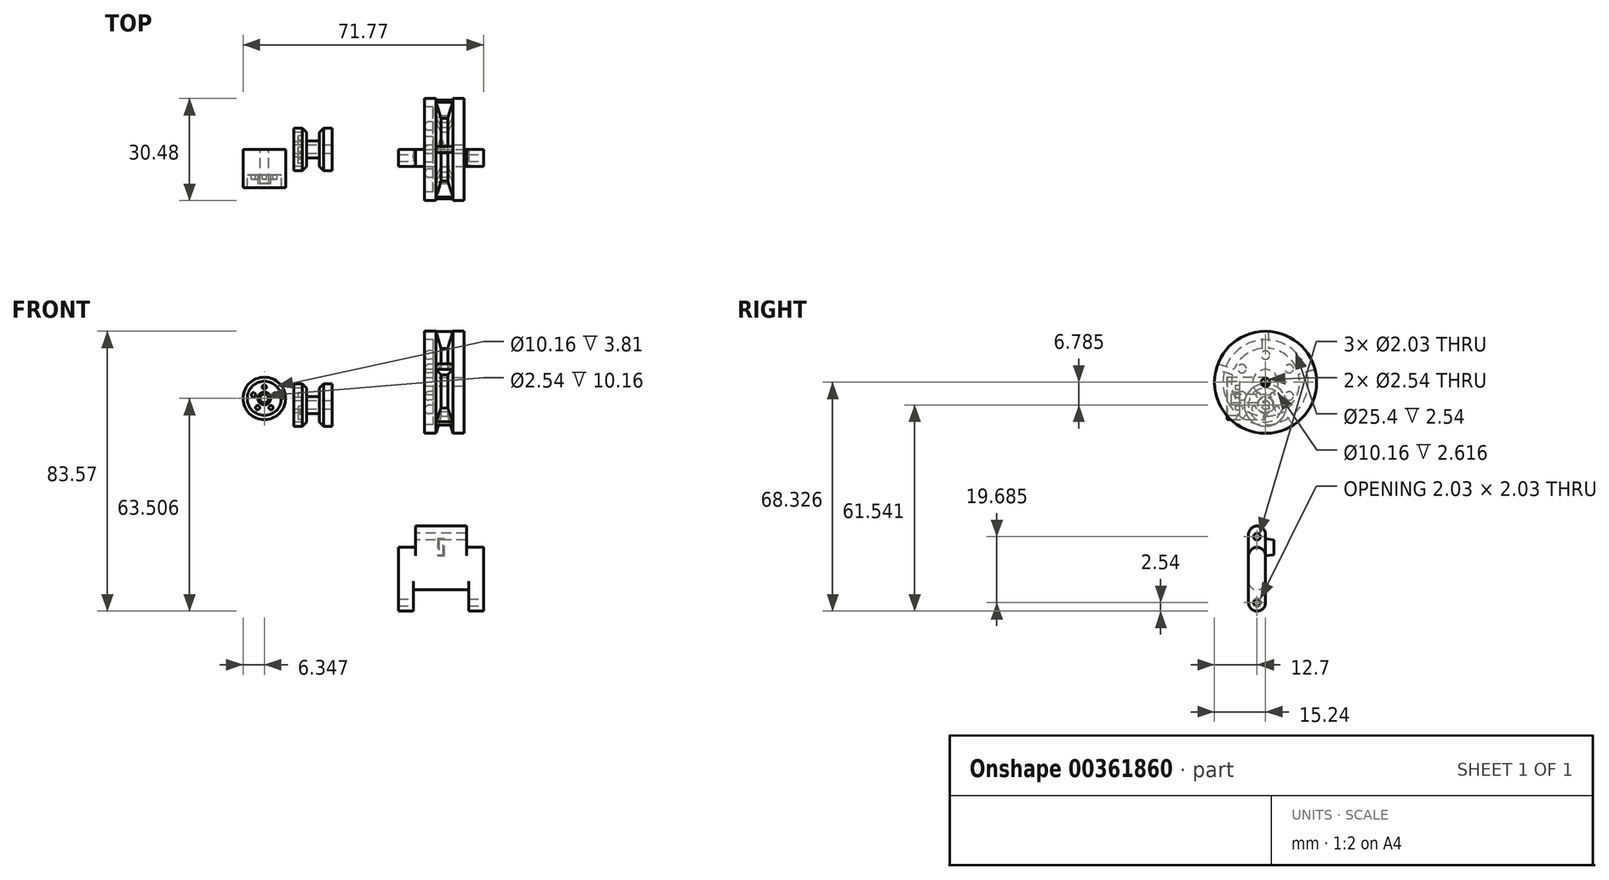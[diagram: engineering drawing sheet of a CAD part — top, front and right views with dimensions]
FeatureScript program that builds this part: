
annotation { "Feature Type Name" : "Feature", "Feature Type Description" : "" }
export const myFeature = defineFeature(function(context is Context, id is Id, definition is map)
    precondition{}
    {
        {
            var Q0;
            Q0=qCreatedBy(makeId("Front.planeOp"),FACE);
            var sketch = newSketch(context, id + "F0", { "sketchPlane" : qUnion([Q0])});
            skLineSegment(sketch, "E0", {"start": v(0, 6.35) * mm, "end": v(-7.62, 6.35) * mm});
            skLineSegment(sketch, "E1", {"start": v(-7.62, 6.35) * mm, "end": v(-7.62, 0) * mm});
            skLineSegment(sketch, "E2", {"start": v(-7.62, 0) * mm, "end": v(-12.7, 0) * mm});
            skLineSegment(sketch, "E3", {"start": v(-12.7, 0) * mm, "end": v(-12.7, -19.05) * mm});
            skLineSegment(sketch, "E4", {"start": v(-12.7, -19.05) * mm, "end": v(-8.26, -19.05) * mm});
            skLineSegment(sketch, "E5", {"start": v(-8.26, -19.05) * mm, "end": v(-8.26, -12.7) * mm});
            skLineSegment(sketch, "E6", {"start": v(-8.26, -12.7) * mm, "end": v(0, -12.7) * mm});
            skLineSegment(sketch, "E7.MirrorCS", {"start": v(0, 6.35) * mm, "end": v(7.62, 6.35) * mm});
            skLineSegment(sketch, "E8.MirrorCS", {"start": v(7.62, 6.35) * mm, "end": v(7.62, 0) * mm});
            skLineSegment(sketch, "E9.MirrorCS", {"start": v(7.62, 0) * mm, "end": v(12.7, 0) * mm});
            skLineSegment(sketch, "E10.MirrorCS", {"start": v(12.7, 0) * mm, "end": v(12.7, -19.05) * mm});
            skLineSegment(sketch, "E11.MirrorCS", {"start": v(12.7, -19.05) * mm, "end": v(8.26, -19.05) * mm});
            skLineSegment(sketch, "E12.MirrorCS", {"start": v(8.26, -12.7) * mm, "end": v(0, -12.7) * mm});
            skLineSegment(sketch, "E13.MirrorCS", {"start": v(8.26, -19.05) * mm, "end": v(8.26, -12.7) * mm});
            skSolve(sketch);
        }
        {
            var Q0;
            Q0=makeQuery(id+"F0.imprint","IMPRINT",FACE,{"disambiguationData":[TD([[makeQuery(id+"F0.imprint","IMPRINT",EDGE,{"derivedFrom":sQuery(id+"F0.wireOp",EDGE,"E0")}),1.0]])]});
            extrude(context, id + "F1", {"entities" : qUnion([Q0]), "depth" : 5.08 * mm});
        }
        {
            var Q0;
            Q0=makeQuery(id+"F1.opExtrude","SWEPT_FACE",FACE,{"disambiguationData":[OSD([sQuery(id+"F0.wireOp",EDGE,"E1")])]});
            var sketch = newSketch(context, id + "F2", { "sketchPlane" : qUnion([Q0])});
            skCircle(sketch, "E14", {"center": v(2.54, 3.17) * mm, "radius": 1.02 * mm});
            skPoint(sketch, "E14.centerSnap0", {"position": v(2.54, 6.35) * mm});
            skPoint(sketch, "E14.centerSnap1", {"position": v(5.08, 3.17) * mm});
            skSolve(sketch);
        }
        {
            var Q0;
            Q0=makeQuery(id+"F2.imprint","IMPRINT",FACE,{"disambiguationData":[TD([[makeQuery(id+"F2.imprint","IMPRINT",EDGE,{"derivedFrom":sQuery(id+"F2.wireOp",EDGE,"E14")}),1.0]])]});
            extrude(context, id + "F3", {"entities" : qUnion([Q0]), "operationType" : NewBodyOperationType.REMOVE, "oppositeDirection" : true, "depth" : 25.4 * mm});
        }
        {
            var Q0;
            Q0=makeQuery(id+"F1.opExtrude","CAP_EDGE",EDGE,{"disambiguationData":[OSD([sQuery(id+"F0.wireOp",EDGE,"E0"),sQuery(id+"F0.wireOp",EDGE,"E7.MirrorCS")])],"isStart":false});
            var Q1;
            Q1=makeQuery(id+"F1.opExtrude","CAP_EDGE",EDGE,{"disambiguationData":[OSD([sQuery(id+"F0.wireOp",EDGE,"E0"),sQuery(id+"F0.wireOp",EDGE,"E7.MirrorCS")])],"isStart":true});
            var Q2;
            Q2=makeQuery(id+"F1.opExtrude","CAP_EDGE",EDGE,{"disambiguationData":[OSD([sQuery(id+"F0.wireOp",EDGE,"E2")])],"isStart":false});
            var Q3;
            Q3=makeQuery(id+"F1.opExtrude","CAP_EDGE",EDGE,{"disambiguationData":[OSD([sQuery(id+"F0.wireOp",EDGE,"E2")])],"isStart":true});
            var Q4;
            Q4=makeQuery(id+"F1.opExtrude","CAP_EDGE",EDGE,{"disambiguationData":[OSD([sQuery(id+"F0.wireOp",EDGE,"E9.MirrorCS")])],"isStart":false});
            var Q5;
            Q5=makeQuery(id+"F1.opExtrude","CAP_EDGE",EDGE,{"disambiguationData":[OSD([sQuery(id+"F0.wireOp",EDGE,"E9.MirrorCS")])],"isStart":true});
            var Q6;
            Q6=makeQuery(id+"F1.opExtrude","CAP_EDGE",EDGE,{"disambiguationData":[OSD([sQuery(id+"F0.wireOp",EDGE,"E11.MirrorCS")])],"isStart":false});
            var Q7;
            Q7=makeQuery(id+"F1.opExtrude","CAP_EDGE",EDGE,{"disambiguationData":[OSD([sQuery(id+"F0.wireOp",EDGE,"E11.MirrorCS")])],"isStart":true});
            var Q8;
            Q8=makeQuery(id+"F1.opExtrude","CAP_EDGE",EDGE,{"disambiguationData":[OSD([sQuery(id+"F0.wireOp",EDGE,"E4")])],"isStart":true});
            var Q9;
            Q9=makeQuery(id+"F1.opExtrude","CAP_EDGE",EDGE,{"disambiguationData":[OSD([sQuery(id+"F0.wireOp",EDGE,"E4")])],"isStart":false});
            var Q10;
            Q10=makeQuery(id+"F1.opExtrude","CAP_EDGE",EDGE,{"disambiguationData":[OSD([sQuery(id+"F0.wireOp",EDGE,"E6"),sQuery(id+"F0.wireOp",EDGE,"E12.MirrorCS")])],"isStart":false});
            var Q11;
            Q11=makeQuery(id+"F1.opExtrude","CAP_EDGE",EDGE,{"disambiguationData":[OSD([sQuery(id+"F0.wireOp",EDGE,"E6"),sQuery(id+"F0.wireOp",EDGE,"E12.MirrorCS")])],"isStart":true});
            fillet(context, id + "F4", {"entities" : qUnion([Q0, Q1, Q2, Q3, Q4, Q5, Q6, Q7, Q8, Q9, Q10, Q11]), "radius" : 2.54 * mm, "tangentPropagation" : true, "allowEdgeOverflow" : false});
        }
        {
            var Q0;
            Q0=makeQuery(id+"F1.opExtrude","SWEPT_FACE",FACE,{"disambiguationData":[OSD([sQuery(id+"F0.wireOp",EDGE,"E5")])]});
            var sketch = newSketch(context, id + "F5", { "sketchPlane" : qUnion([Q0])});
            skCircle(sketch, "E15", {"center": v(-2.54, -16.51) * mm, "radius": 1.02 * mm});
            skSolve(sketch);
        }
        {
            var Q0;
            Q0=makeQuery(id+"F5.imprint","IMPRINT",FACE,{"disambiguationData":[TD([[makeQuery(id+"F5.imprint","IMPRINT",EDGE,{"derivedFrom":sQuery(id+"F5.wireOp",EDGE,"E15")}),1.0]])]});
            extrude(context, id + "F6", {"entities" : qUnion([Q0]), "operationType" : NewBodyOperationType.REMOVE, "endBound" : BoundingType.SYMMETRIC, "oppositeDirection" : true, "depth" : 50.8 * mm});
        }
        {
            var Q0;
            Q0=makeQuery(id+"F1.opExtrude","CAP_FACE",FACE,{"disambiguationData":[OSD([sQuery(id+"F0.wireOp",EDGE,"E0"),sQuery(id+"F0.wireOp",EDGE,"E1"),sQuery(id+"F0.wireOp",EDGE,"E2"),sQuery(id+"F0.wireOp",EDGE,"E3"),sQuery(id+"F0.wireOp",EDGE,"E4"),sQuery(id+"F0.wireOp",EDGE,"E5"),sQuery(id+"F0.wireOp",EDGE,"E6"),sQuery(id+"F0.wireOp",EDGE,"E7.MirrorCS"),sQuery(id+"F0.wireOp",EDGE,"E8.MirrorCS"),sQuery(id+"F0.wireOp",EDGE,"E9.MirrorCS"),sQuery(id+"F0.wireOp",EDGE,"E10.MirrorCS"),sQuery(id+"F0.wireOp",EDGE,"E11.MirrorCS"),sQuery(id+"F0.wireOp",EDGE,"E12.MirrorCS"),sQuery(id+"F0.wireOp",EDGE,"E13.MirrorCS")])],"isStart":true});
            var sketch = newSketch(context, id + "F7", { "sketchPlane" : qUnion([Q0])});
            skLineSegment(sketch, "E16", {"start": v(-7.62, -1.08) * mm, "end": v(7.62, -1.08) * mm});
            skLineSegment(sketch, "E17", {"start": v(7.62, -1.08) * mm, "end": v(7.62, -2.54) * mm});
            skLineSegment(sketch, "E18", {"start": v(7.62, -2.54) * mm, "end": v(12.7, -2.54) * mm});
            skLineSegment(sketch, "E19", {"start": v(12.7, -2.54) * mm, "end": v(12.7, -4.94) * mm});
            skLineSegment(sketch, "E20", {"start": v(12.7, -4.94) * mm, "end": v(8.26, -4.94) * mm});
            skLineSegment(sketch, "E21", {"start": v(8.26, -10.16) * mm, "end": v(8.26, -4.94) * mm});
            skLineSegment(sketch, "E22", {"start": v(8.26, -10.16) * mm, "end": v(-8.26, -10.16) * mm});
            skLineSegment(sketch, "E23", {"start": v(-8.26, -4.94) * mm, "end": v(-8.26, -10.16) * mm});
            skLineSegment(sketch, "E24", {"start": v(-8.26, -4.94) * mm, "end": v(-12.7, -4.94) * mm});
            skLineSegment(sketch, "E25", {"start": v(-12.7, -4.94) * mm, "end": v(-12.7, -2.54) * mm});
            skLineSegment(sketch, "E26", {"start": v(-12.7, -2.54) * mm, "end": v(-7.62, -2.54) * mm});
            skLineSegment(sketch, "E27", {"start": v(-7.62, -2.54) * mm, "end": v(-7.62, -1.08) * mm});
            skSolve(sketch);
        }
        {
            var Q0;
            {var subQ0=sQuery(id+"F7.wireOp",EDGE,"E16");Q0=makeQuery(id+"F7.imprint","IMPRINT",FACE,{"disambiguationData":[TD([[makeQuery(id+"F7.imprint","IMPRINT",EDGE,{"derivedFrom":subQ0}),1.0]])]});}
            var sketch = newSketch(context, id + "F8", { "sketchPlane" : qUnion([Q0])});
            skLineSegment(sketch, "E28.bottom", {"start": v(-1.02, 2.54) * mm, "end": v(1.02, 2.54) * mm});
            skLineSegment(sketch, "E28.top", {"start": v(-1.02, -2.54) * mm, "end": v(1.02, -2.54) * mm});
            skLineSegment(sketch, "E28.left", {"start": v(-1.02, 2.54) * mm, "end": v(-1.02, -2.54) * mm});
            skLineSegment(sketch, "E28.right", {"start": v(1.02, 2.54) * mm, "end": v(1.02, -2.54) * mm});
            skPoint(sketch, "E28.middle", {"position": v(0, 0) * mm});
            skSolve(sketch);
        }
        {
            var Q0;
            {var subQ0=sQuery(id+"F8.wireOp",EDGE,"E28.bottom");Q0=makeQuery(id+"F8.imprint","IMPRINT",FACE,{"disambiguationData":[TD([[makeQuery(id+"F8.imprint","IMPRINT",EDGE,{"derivedFrom":subQ0}),-1.0]])]});}
            var Q1;
            {var subQ0=sQuery(id+"F8.wireOp",EDGE,"E28.top");Q1=makeQuery(id+"F8.imprint","IMPRINT",FACE,{"disambiguationData":[TD([[makeQuery(id+"F8.imprint","IMPRINT",EDGE,{"derivedFrom":subQ0}),1.0]])]});}
            extrude(context, id + "F9", {"entities" : qUnion([Q0, Q1]), "operationType" : NewBodyOperationType.ADD, "depth" : 2.54 * mm, "hasDraft" : true, "draftAngle" : 8 * degree, "draftPullDirection" : true});
        }
        {
            var Q0;
            Q0=qCreatedBy(makeId("Front.planeOp"),FACE);
            var sketch = newSketch(context, id + "F10", { "sketchPlane" : qUnion([Q0])});
            skLineSegment(sketch, "E29", {"start": v(-4.88, 49.28) * mm, "end": v(-4.88, 64.52) * mm});
            skLineSegment(sketch, "E30", {"start": v(-4.88, 64.52) * mm, "end": v(-1.52, 64.52) * mm});
            skLineSegment(sketch, "E31", {"start": v(-1.52, 64.52) * mm, "end": v(0, 59.44) * mm});
            skLineSegment(sketch, "E32", {"start": v(0, 59.44) * mm, "end": v(2.03, 59.44) * mm});
            skLineSegment(sketch, "E33", {"start": v(2.03, 59.44) * mm, "end": v(3.56, 64.52) * mm});
            skLineSegment(sketch, "E34", {"start": v(3.56, 64.52) * mm, "end": v(6.91, 64.52) * mm});
            skLineSegment(sketch, "E35", {"start": v(6.91, 64.52) * mm, "end": v(6.91, 49.28) * mm});
            skLineSegment(sketch, "E36", {"start": v(6.91, 49.28) * mm, "end": v(-4.88, 49.28) * mm});
            skSolve(sketch);
        }
        {
            var Q0;
            Q0=makeQuery(id+"F10.imprint","IMPRINT",FACE,{"disambiguationData":[TD([[makeQuery(id+"F10.imprint","IMPRINT",EDGE,{"derivedFrom":sQuery(id+"F10.wireOp",EDGE,"E29")}),-1.0]])]});
            var Q1;
            Q1=sQuery(id+"F10.wireOp",EDGE,"E36");
            revolve(context, id + "F11", {"entities" : qUnion([Q0]), "axis" : qUnion([Q1]), "revolveType" : RevolveType.FULL});
        }
        {
            var Q0;
            Q0=makeQuery(id+"F11.opRevolve","SWEPT_FACE",FACE,{"disambiguationData":[OSD([sQuery(id+"F10.wireOp",EDGE,"E29")])]});
            var sketch = newSketch(context, id + "F12", { "sketchPlane" : qUnion([Q0])});
            skCircle(sketch, "E37", {"center": v(0, 49.28) * mm, "radius": 1.27 * mm});
            skCircle(sketch, "E38", {"center": v(0, 49.28) * mm, "radius": 3.81 * mm});
            skCircle(sketch, "E39", {"center": v(0, 49.28) * mm, "radius": 12.7 * mm});
            skSolve(sketch);
        }
        {
            var Q0;
            Q0=makeQuery(id+"F12.imprint","IMPRINT",FACE,{"disambiguationData":[TD([[makeQuery(id+"F12.imprint","IMPRINT",EDGE,{"derivedFrom":sQuery(id+"F12.wireOp",EDGE,"E38")}),-1.0]])]});
            extrude(context, id + "F13", {"entities" : qUnion([Q0]), "operationType" : NewBodyOperationType.REMOVE, "oppositeDirection" : true, "depth" : 2.54 * mm});
        }
        {
            var Q0;
            Q0=makeQuery(id+"F12.imprint","IMPRINT",FACE,{"disambiguationData":[TD([[makeQuery(id+"F12.imprint","IMPRINT",EDGE,{"derivedFrom":sQuery(id+"F12.wireOp",EDGE,"E37")}),1.0]])]});
            extrude(context, id + "F14", {"entities" : qUnion([Q0]), "operationType" : NewBodyOperationType.REMOVE, "oppositeDirection" : true, "depth" : 25.4 * mm});
        }
        {
            var Q0;
            Q0=makeQuery(id+"F12.imprint","IMPRINT",FACE,{"disambiguationData":[TD([[makeQuery(id+"F12.imprint","IMPRINT",EDGE,{"derivedFrom":sQuery(id+"F12.wireOp",EDGE,"E38")}),-1.0]])]});
            var sketch = newSketch(context, id + "F15", { "sketchPlane" : qUnion([Q0])});
            skCircle(sketch, "E40", {"center": v(0, 57.4) * mm, "radius": 1.27 * mm});
            skCircle(sketch, "E41.1.0", {"center": v(-7.04, 53.34) * mm, "radius": 1.27 * mm});
            skCircle(sketch, "E41.2.0", {"center": v(-7.04, 45.21) * mm, "radius": 1.27 * mm});
            skPoint(sketch, "E41.center", {"position": v(0, 49.28) * mm});
            skCircle(sketch, "E42.1.3.0", {"center": v(0, 41.15) * mm, "radius": 1.27 * mm});
            skCircle(sketch, "E42.1.4.0", {"center": v(7.04, 45.21) * mm, "radius": 1.27 * mm});
            skCircle(sketch, "E42.1.5.0", {"center": v(7.04, 53.34) * mm, "radius": 1.27 * mm});
            skSolve(sketch);
        }
        {
            var Q0;
            Q0=makeQuery(id+"F15.imprint","IMPRINT",FACE,{"disambiguationData":[TD([[makeQuery(id+"F15.imprint","IMPRINT",EDGE,{"derivedFrom":sQuery(id+"F15.wireOp",EDGE,"E41.1.0")}),1.0]])]});
            var Q1;
            Q1=makeQuery(id+"F15.imprint","IMPRINT",FACE,{"disambiguationData":[TD([[makeQuery(id+"F15.imprint","IMPRINT",EDGE,{"derivedFrom":sQuery(id+"F15.wireOp",EDGE,"E40")}),1.0]])]});
            var Q2;
            Q2=makeQuery(id+"F15.imprint","IMPRINT",FACE,{"disambiguationData":[TD([[makeQuery(id+"F15.imprint","IMPRINT",EDGE,{"derivedFrom":sQuery(id+"F15.wireOp",EDGE,"E42.1.5.0")}),1.0]])]});
            var Q3;
            Q3=makeQuery(id+"F15.imprint","IMPRINT",FACE,{"disambiguationData":[TD([[makeQuery(id+"F15.imprint","IMPRINT",EDGE,{"derivedFrom":sQuery(id+"F15.wireOp",EDGE,"E41.2.0")}),1.0]])]});
            var Q4;
            Q4=makeQuery(id+"F15.imprint","IMPRINT",FACE,{"disambiguationData":[TD([[makeQuery(id+"F15.imprint","IMPRINT",EDGE,{"derivedFrom":sQuery(id+"F15.wireOp",EDGE,"E42.1.3.0")}),1.0]])]});
            var Q5;
            Q5=makeQuery(id+"F15.imprint","IMPRINT",FACE,{"disambiguationData":[TD([[makeQuery(id+"F15.imprint","IMPRINT",EDGE,{"derivedFrom":sQuery(id+"F15.wireOp",EDGE,"E42.1.4.0")}),1.0]])]});
            extrude(context, id + "F16", {"entities" : qUnion([Q0, Q1, Q2, Q3, Q4, Q5]), "operationType" : NewBodyOperationType.ADD, "oppositeDirection" : true, "depth" : 2.54 * mm});
        }
        {
            var Q0;
            Q0=makeQuery(id+"F16.opExtrude","CAP_FACE",FACE,{"disambiguationData":[OSD([sQuery(id+"F15.wireOp",EDGE,"E41.1.0")])],"isStart":true});
            var Q1;
            Q1=makeQuery(id+"F16.opExtrude","CAP_FACE",FACE,{"disambiguationData":[OSD([sQuery(id+"F15.wireOp",EDGE,"E41.2.0")])],"isStart":true});
            var Q2;
            Q2=makeQuery(id+"F16.opExtrude","CAP_FACE",FACE,{"disambiguationData":[OSD([sQuery(id+"F15.wireOp",EDGE,"E42.1.3.0")])],"isStart":true});
            var Q3;
            Q3=makeQuery(id+"F16.opExtrude","CAP_FACE",FACE,{"disambiguationData":[OSD([sQuery(id+"F15.wireOp",EDGE,"E42.1.4.0")])],"isStart":true});
            var Q4;
            Q4=makeQuery(id+"F16.opExtrude","CAP_FACE",FACE,{"disambiguationData":[OSD([sQuery(id+"F15.wireOp",EDGE,"E42.1.5.0")])],"isStart":true});
            var Q5;
            Q5=makeQuery(id+"F16.opExtrude","CAP_FACE",FACE,{"disambiguationData":[OSD([sQuery(id+"F15.wireOp",EDGE,"E40")])],"isStart":true});
            fillet(context, id + "F17", {"entities" : qUnion([Q0, Q1, Q2, Q3, Q4, Q5]), "radius" : 1.27 * mm, "tangentPropagation" : true, "allowEdgeOverflow" : false});
        }
        {
            var Q0;
            Q0=makeQuery(id+"F11.opRevolve","SWEPT_FACE",FACE,{"disambiguationData":[OSD([sQuery(id+"F10.wireOp",EDGE,"E35")])]});
            var sketch = newSketch(context, id + "F18", { "sketchPlane" : qUnion([Q0])});
            skLineSegment(sketch, "E43", {"start": v(-0.89, 64.45) * mm, "end": v(0.87, 64.45) * mm});
            skLineSegment(sketch, "E44", {"start": v(0.87, 64.45) * mm, "end": v(0.87, 57.17) * mm});
            skLineSegment(sketch, "E45", {"start": v(0.87, 57.17) * mm, "end": v(-0.95, 57.17) * mm});
            skLineSegment(sketch, "E46", {"start": v(-0.95, 57.17) * mm, "end": v(-0.89, 64.45) * mm});
            skLineSegment(sketch, "E47.1.0", {"start": v(-14.7, 53.12) * mm, "end": v(-14.16, 54.8) * mm});
            skLineSegment(sketch, "E47.1.1", {"start": v(-14.16, 54.8) * mm, "end": v(-7.24, 52.54) * mm});
            skLineSegment(sketch, "E47.1.2", {"start": v(-7.24, 52.54) * mm, "end": v(-7.8, 50.81) * mm});
            skLineSegment(sketch, "E47.1.3", {"start": v(-7.8, 50.81) * mm, "end": v(-14.7, 53.12) * mm});
            skLineSegment(sketch, "E47.2.0", {"start": v(-8.2, 36.48) * mm, "end": v(-9.62, 37.5) * mm});
            skLineSegment(sketch, "E47.2.1", {"start": v(-9.62, 37.5) * mm, "end": v(-5.34, 43.4) * mm});
            skLineSegment(sketch, "E47.2.2", {"start": v(-5.34, 43.4) * mm, "end": v(-3.87, 42.33) * mm});
            skLineSegment(sketch, "E47.2.3", {"start": v(-3.87, 42.33) * mm, "end": v(-8.2, 36.48) * mm});
            skPoint(sketch, "E47.center", {"position": v(0, 49.28) * mm});
            skLineSegment(sketch, "E48.1.3.0", {"start": v(9.64, 37.52) * mm, "end": v(8.22, 36.49) * mm});
            skLineSegment(sketch, "E48.3.3.0", {"start": v(8.22, 36.49) * mm, "end": v(3.94, 42.38) * mm});
            skLineSegment(sketch, "E48.6.3.0", {"start": v(3.94, 42.38) * mm, "end": v(5.4, 43.45) * mm});
            skLineSegment(sketch, "E48.9.3.0", {"start": v(5.4, 43.45) * mm, "end": v(9.64, 37.52) * mm});
            skLineSegment(sketch, "E48.1.4.0", {"start": v(14.16, 54.8) * mm, "end": v(14.7, 53.14) * mm});
            skLineSegment(sketch, "E48.3.4.0", {"start": v(14.7, 53.14) * mm, "end": v(7.77, 50.89) * mm});
            skLineSegment(sketch, "E48.6.4.0", {"start": v(7.77, 50.89) * mm, "end": v(7.21, 52.62) * mm});
            skLineSegment(sketch, "E48.9.4.0", {"start": v(7.21, 52.62) * mm, "end": v(14.16, 54.8) * mm});
            skSolve(sketch);
        }
        {
            var Q0;
            Q0=makeQuery(id+"F18.imprint","IMPRINT",FACE,{"disambiguationData":[TD([[makeQuery(id+"F18.imprint","IMPRINT",EDGE,{"derivedFrom":sQuery(id+"F18.wireOp",EDGE,"E43")}),-1.0]])]});
            var Q1;
            Q1=makeQuery(id+"F18.imprint","IMPRINT",FACE,{"disambiguationData":[TD([[makeQuery(id+"F18.imprint","IMPRINT",EDGE,{"derivedFrom":sQuery(id+"F18.wireOp",EDGE,"E47.1.0")}),-1.0]])]});
            var Q2;
            Q2=makeQuery(id+"F18.imprint","IMPRINT",FACE,{"disambiguationData":[TD([[makeQuery(id+"F18.imprint","IMPRINT",EDGE,{"derivedFrom":sQuery(id+"F18.wireOp",EDGE,"E47.2.0")}),-1.0]])]});
            var Q3;
            Q3=makeQuery(id+"F18.imprint","IMPRINT",FACE,{"disambiguationData":[TD([[makeQuery(id+"F18.imprint","IMPRINT",EDGE,{"derivedFrom":sQuery(id+"F18.wireOp",EDGE,"E48.1.3.0")}),-1.0]])]});
            var Q4;
            Q4=makeQuery(id+"F18.imprint","IMPRINT",FACE,{"disambiguationData":[TD([[makeQuery(id+"F18.imprint","IMPRINT",EDGE,{"derivedFrom":sQuery(id+"F18.wireOp",EDGE,"E48.1.4.0")}),-1.0]])]});
            extrude(context, id + "F19", {"entities" : qUnion([Q0, Q1, Q2, Q3, Q4]), "operationType" : NewBodyOperationType.ADD, "oppositeDirection" : true, "depth" : 8.9 * mm});
        }
        {
            var Q0;
            Q0=qCreatedBy(makeId("Front.planeOp"),FACE);
            var sketch = newSketch(context, id + "F20", { "sketchPlane" : qUnion([Q0])});
            skCircle(sketch, "E49", {"center": v(-52.72, 44.46) * mm, "radius": 6.35 * mm});
            skCircle(sketch, "E50", {"center": v(-52.72, 44.46) * mm, "radius": 1.27 * mm});
            skCircle(sketch, "E51", {"center": v(-52.72, 44.46) * mm, "radius": 1.9 * mm});
            skCircle(sketch, "E52", {"center": v(-52.72, 44.46) * mm, "radius": 5.08 * mm});
            skCircle(sketch, "E53", {"center": v(-52.72, 47.85) * mm, "radius": 0.64 * mm});
            skCircle(sketch, "E54.1.0", {"center": v(-55.95, 45.5) * mm, "radius": 0.64 * mm});
            skCircle(sketch, "E54.2.0", {"center": v(-54.72, 41.7) * mm, "radius": 0.64 * mm});
            skCircle(sketch, "E55.1.3.0", {"center": v(-50.73, 41.7) * mm, "radius": 0.64 * mm});
            skCircle(sketch, "E55.1.4.0", {"center": v(-49.5, 45.5) * mm, "radius": 0.64 * mm});
            skSolve(sketch);
        }
        {
            var Q0;
            Q0=makeQuery(id+"F20.imprint","IMPRINT",FACE,{"disambiguationData":[TD([[makeQuery(id+"F20.imprint","IMPRINT",EDGE,{"derivedFrom":sQuery(id+"F20.wireOp",EDGE,"E49")}),1.0]])]});
            extrude(context, id + "F21", {"entities" : qUnion([Q0]), "depth" : 11.43 * mm});
        }
        {
            var Q0;
            Q0=makeQuery(id+"F20.imprint","IMPRINT",FACE,{"disambiguationData":[TD([[makeQuery(id+"F20.imprint","IMPRINT",EDGE,{"derivedFrom":sQuery(id+"F20.wireOp",EDGE,"E51")}),-1.0]])]});
            extrude(context, id + "F22", {"entities" : qUnion([Q0]), "operationType" : NewBodyOperationType.ADD, "depth" : 7.62 * mm});
        }
        {
            var Q0;
            Q0=makeQuery(id+"F20.imprint","IMPRINT",FACE,{"disambiguationData":[TD([[makeQuery(id+"F20.imprint","IMPRINT",EDGE,{"derivedFrom":sQuery(id+"F20.wireOp",EDGE,"E53")}),1.0]])]});
            var Q1;
            Q1=makeQuery(id+"F20.imprint","IMPRINT",FACE,{"disambiguationData":[TD([[makeQuery(id+"F20.imprint","IMPRINT",EDGE,{"derivedFrom":sQuery(id+"F20.wireOp",EDGE,"E54.1.0")}),1.0]])]});
            var Q2;
            Q2=makeQuery(id+"F20.imprint","IMPRINT",FACE,{"disambiguationData":[TD([[makeQuery(id+"F20.imprint","IMPRINT",EDGE,{"derivedFrom":sQuery(id+"F20.wireOp",EDGE,"E54.2.0")}),1.0]])]});
            var Q3;
            Q3=makeQuery(id+"F20.imprint","IMPRINT",FACE,{"disambiguationData":[TD([[makeQuery(id+"F20.imprint","IMPRINT",EDGE,{"derivedFrom":sQuery(id+"F20.wireOp",EDGE,"E55.1.3.0")}),1.0]])]});
            var Q4;
            Q4=makeQuery(id+"F20.imprint","IMPRINT",FACE,{"disambiguationData":[TD([[makeQuery(id+"F20.imprint","IMPRINT",EDGE,{"derivedFrom":sQuery(id+"F20.wireOp",EDGE,"E55.1.4.0")}),1.0]])]});
            extrude(context, id + "F23", {"entities" : qUnion([Q0, Q1, Q2, Q3, Q4]), "operationType" : NewBodyOperationType.ADD, "depth" : 8.9 * mm});
        }
        {
            var Q0;
            Q0=makeQuery(id+"F20.imprint","IMPRINT",FACE,{"disambiguationData":[TD([[makeQuery(id+"F20.imprint","IMPRINT",EDGE,{"derivedFrom":sQuery(id+"F20.wireOp",EDGE,"E50")}),-1.0]])]});
            extrude(context, id + "F24", {"entities" : qUnion([Q0]), "operationType" : NewBodyOperationType.ADD, "depth" : 10.16 * mm});
        }
        {
            var Q0;
            Q0=qCreatedBy(makeId("Front.planeOp"),FACE);
            var sketch = newSketch(context, id + "F25", { "sketchPlane" : qUnion([Q0])});
            skLineSegment(sketch, "E56", {"start": v(-43.93, 43.73) * mm, "end": v(-43.93, 48.84) * mm});
            skLineSegment(sketch, "E57", {"start": v(-43.93, 48.84) * mm, "end": v(-40.12, 48.84) * mm});
            skLineSegment(sketch, "E58", {"start": v(-40.12, 48.84) * mm, "end": v(-40.12, 45.03) * mm});
            skLineSegment(sketch, "E59", {"start": v(-40.12, 45.03) * mm, "end": v(-36.3, 45.03) * mm});
            skLineSegment(sketch, "E60", {"start": v(-36.3, 45.03) * mm, "end": v(-36.3, 48.84) * mm});
            skLineSegment(sketch, "E61", {"start": v(-36.3, 48.84) * mm, "end": v(-32.5, 48.84) * mm});
            skLineSegment(sketch, "E62", {"start": v(-32.5, 48.84) * mm, "end": v(-32.5, 42.5) * mm});
            skLineSegment(sketch, "E63", {"start": v(-32.5, 42.5) * mm, "end": v(-43.93, 42.5) * mm});
            skLineSegment(sketch, "E64", {"start": v(-43.93, 42.5) * mm, "end": v(-43.93, 43.73) * mm});
            skSolve(sketch);
        }
        {
            var Q0;
            Q0=makeQuery(id+"F25.imprint","IMPRINT",FACE,{"disambiguationData":[TD([[makeQuery(id+"F25.imprint","IMPRINT",EDGE,{"derivedFrom":sQuery(id+"F25.wireOp",EDGE,"E56")}),-1.0]])]});
            var Q1;
            Q1=sQuery(id+"F25.wireOp",EDGE,"E63");
            revolve(context, id + "F26", {"entities" : qUnion([Q0]), "axis" : qUnion([Q1]), "revolveType" : RevolveType.FULL});
        }
        {
            var Q0;
            Q0=makeQuery(id+"F26.opRevolve","SWEPT_FACE",FACE,{"disambiguationData":[OSD([sQuery(id+"F25.wireOp",EDGE,"E56"),sQuery(id+"F25.wireOp",EDGE,"E64")])]});
            var sketch = newSketch(context, id + "F27", { "sketchPlane" : qUnion([Q0])});
            skCircle(sketch, "E65", {"center": v(0, 42.5) * mm, "radius": 1.27 * mm});
            skCircle(sketch, "E66", {"center": v(0, 42.5) * mm, "radius": 2.29 * mm});
            skCircle(sketch, "E67", {"center": v(0, 42.5) * mm, "radius": 5.08 * mm});
            skCircle(sketch, "E68", {"center": v(0, 38.9) * mm, "radius": 0.71 * mm});
            skCircle(sketch, "E69.1.0", {"center": v(3.42, 41.38) * mm, "radius": 0.71 * mm});
            skCircle(sketch, "E69.2.0", {"center": v(2.12, 45.4) * mm, "radius": 0.71 * mm});
            skCircle(sketch, "E70.1.3.0", {"center": v(-2.12, 45.4) * mm, "radius": 0.71 * mm});
            skCircle(sketch, "E70.1.4.0", {"center": v(-3.42, 41.38) * mm, "radius": 0.71 * mm});
            skSolve(sketch);
        }
        {
            var Q0;
            Q0=makeQuery(id+"F27.imprint","IMPRINT",FACE,{"disambiguationData":[TD([[makeQuery(id+"F27.imprint","IMPRINT",EDGE,{"derivedFrom":sQuery(id+"F27.wireOp",EDGE,"E66")}),-1.0]])]});
            extrude(context, id + "F28", {"entities" : qUnion([Q0]), "operationType" : NewBodyOperationType.REMOVE, "oppositeDirection" : true, "depth" : 2.62 * mm});
        }
        {
            var Q0;
            Q0=makeQuery(id+"F27.imprint","IMPRINT",FACE,{"disambiguationData":[TD([[makeQuery(id+"F27.imprint","IMPRINT",EDGE,{"derivedFrom":sQuery(id+"F27.wireOp",EDGE,"E65")}),1.0]])]});
            extrude(context, id + "F29", {"entities" : qUnion([Q0]), "operationType" : NewBodyOperationType.REMOVE, "oppositeDirection" : true, "depth" : 25.4 * mm});
        }
        {
            var Q0;
            Q0=makeQuery(id+"F27.imprint","IMPRINT",FACE,{"disambiguationData":[TD([[makeQuery(id+"F27.imprint","IMPRINT",EDGE,{"derivedFrom":sQuery(id+"F27.wireOp",EDGE,"E70.1.3.0")}),1.0]])]});
            var Q1;
            Q1=makeQuery(id+"F27.imprint","IMPRINT",FACE,{"disambiguationData":[TD([[makeQuery(id+"F27.imprint","IMPRINT",EDGE,{"derivedFrom":sQuery(id+"F27.wireOp",EDGE,"E70.1.4.0")}),1.0]])]});
            var Q2;
            Q2=makeQuery(id+"F27.imprint","IMPRINT",FACE,{"disambiguationData":[TD([[makeQuery(id+"F27.imprint","IMPRINT",EDGE,{"derivedFrom":sQuery(id+"F27.wireOp",EDGE,"E68")}),1.0]])]});
            var Q3;
            Q3=makeQuery(id+"F27.imprint","IMPRINT",FACE,{"disambiguationData":[TD([[makeQuery(id+"F27.imprint","IMPRINT",EDGE,{"derivedFrom":sQuery(id+"F27.wireOp",EDGE,"E69.1.0")}),1.0]])]});
            var Q4;
            Q4=makeQuery(id+"F27.imprint","IMPRINT",FACE,{"disambiguationData":[TD([[makeQuery(id+"F27.imprint","IMPRINT",EDGE,{"derivedFrom":sQuery(id+"F27.wireOp",EDGE,"E69.2.0")}),1.0]])]});
            extrude(context, id + "F30", {"entities" : qUnion([Q0, Q1, Q2, Q3, Q4]), "operationType" : NewBodyOperationType.REMOVE, "oppositeDirection" : true, "depth" : 1.27 * mm});
        }
        {
            var Q0;
            Q0=makeQuery(id+"F26.opRevolve","SWEPT_EDGE",EDGE,{"disambiguationData":[OSD([sQuery(id+"F25.wireOp",EDGE,"E57"),sQuery(id+"F25.wireOp",EDGE,"E58")])]});
            var Q1;
            Q1=makeQuery(id+"F26.opRevolve","SWEPT_EDGE",EDGE,{"disambiguationData":[OSD([sQuery(id+"F25.wireOp",EDGE,"E60"),sQuery(id+"F25.wireOp",EDGE,"E61")])]});
            chamfer(context, id + "F31", {"entities" : qUnion([Q0, Q1]), "width" : 1.27 * mm, "tangentPropagation" : true});
        }
    });
